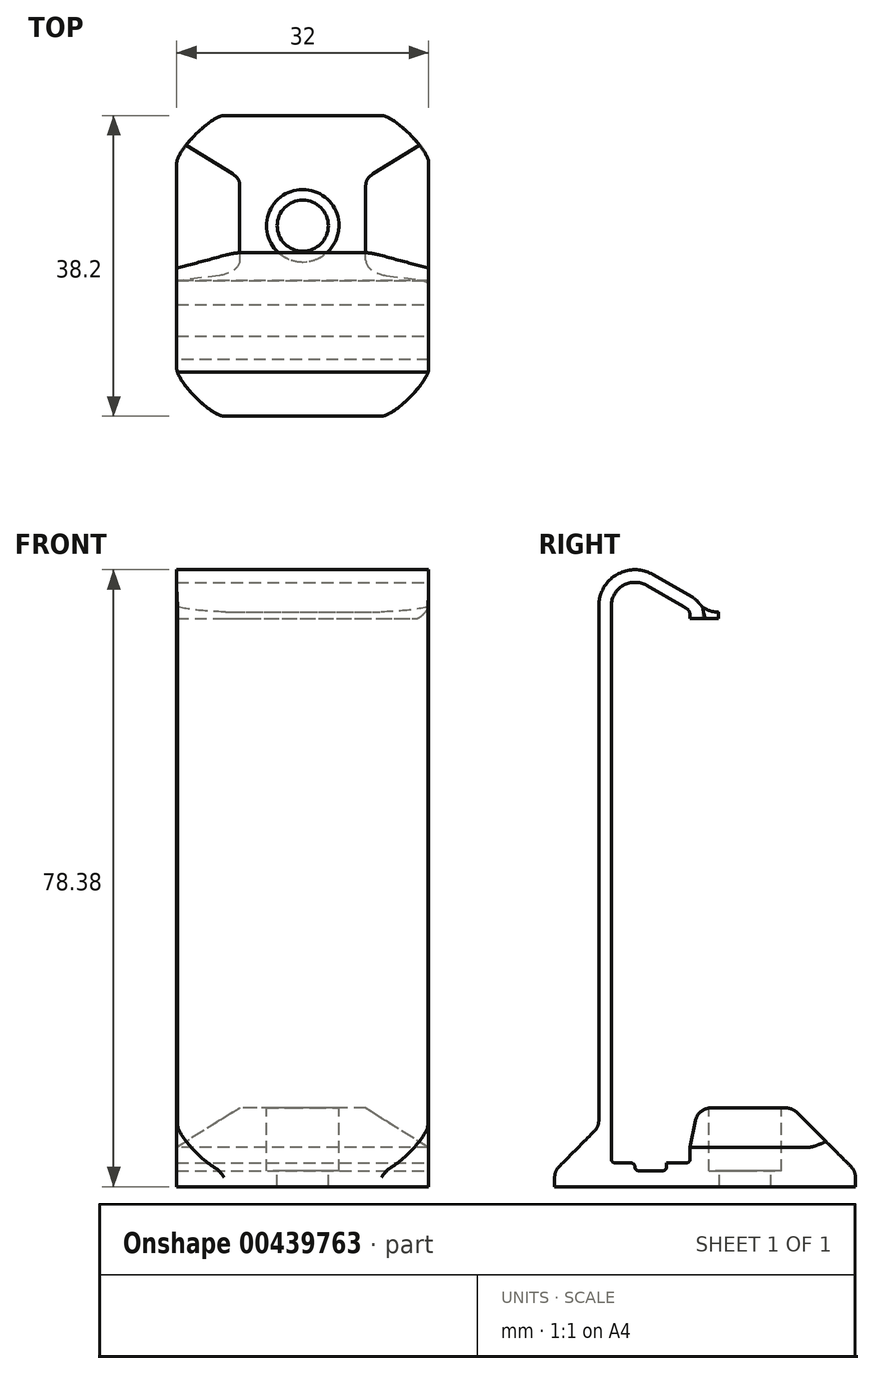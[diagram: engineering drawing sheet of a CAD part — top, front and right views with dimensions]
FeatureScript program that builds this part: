
annotation { "Feature Type Name" : "Feature", "Feature Type Description" : "" }
export const myFeature = defineFeature(function(context is Context, id is Id, definition is map)
    precondition{}
    {
        {
            var Q0;
            Q0=qCreatedBy(makeId("Right.planeOp"),FACE);
            var sketch = newSketch(context, id + "F0", { "sketchPlane" : qUnion([Q0])});
            skLineSegment(sketch, "E0.bottom", {"start": v(-5, 0) * mm, "end": v(5, 0) * mm});
            skLineSegment(sketch, "E0.top", {"start": v(-5, 70.2) * mm, "end": v(5, 70.2) * mm});
            skLineSegment(sketch, "E0.left", {"start": v(-5, 0) * mm, "end": v(-5, 70.2) * mm});
            skLineSegment(sketch, "E0.right", {"start": v(5, 0) * mm, "end": v(5, 70.2) * mm});
            skSolve(sketch);
        }
        {
            var Q0;
            Q0=qCreatedBy(makeId("Right.planeOp"),FACE);
            var sketch = newSketch(context, id + "F1", { "sketchPlane" : qUnion([Q0])});
            skLineSegment(sketch, "E1", {"start": v(-5, 4.6) * mm, "end": v(-6.6, 4.6) * mm});
            skLineSegment(sketch, "E2", {"start": v(-6.6, 4.6) * mm, "end": v(-12.2, -1) * mm});
            skLineSegment(sketch, "E3", {"start": v(-12.2, -1) * mm, "end": v(-12.2, -3) * mm});
            skLineSegment(sketch, "E4", {"start": v(-12.2, -3) * mm, "end": v(26, -3) * mm});
            skLineSegment(sketch, "E5", {"start": v(26, -3) * mm, "end": v(26, -1) * mm});
            skLineSegment(sketch, "E6", {"start": v(26, -1) * mm, "end": v(18, 7) * mm});
            skLineSegment(sketch, "E7", {"start": v(18, 7) * mm, "end": v(5, 7) * mm});
            skLineSegment(sketch, "E8", {"start": v(5, 7) * mm, "end": v(5, 0) * mm});
            skLineSegment(sketch, "E9", {"start": v(5, 0) * mm, "end": v(-5, 0) * mm});
            skLineSegment(sketch, "E10", {"start": v(-5, 0) * mm, "end": v(-5, 4.6) * mm});
            skSolve(sketch);
        }
        {
            var Q0;
            Q0=qSketchRegion(id+"F1",true);
            extrude(context, id + "F2", {"entities" : qUnion([Q0]), "endBound" : BoundingType.SYMMETRIC, "depth" : 32 * mm});
        }
        {
            var Q0;
            Q0=makeQuery(id+"F2.opExtrude","CAP_FACE",FACE,{"disambiguationData":[OSD([sQuery(id+"F1.wireOp",EDGE,"E1"),sQuery(id+"F1.wireOp",EDGE,"E2"),sQuery(id+"F1.wireOp",EDGE,"E3"),sQuery(id+"F1.wireOp",EDGE,"E4"),sQuery(id+"F1.wireOp",EDGE,"E5"),sQuery(id+"F1.wireOp",EDGE,"E6"),sQuery(id+"F1.wireOp",EDGE,"E7"),sQuery(id+"F1.wireOp",EDGE,"E8"),sQuery(id+"F1.wireOp",EDGE,"E9"),sQuery(id+"F1.wireOp",EDGE,"E10")])],"isStart":false});
            var sketch = newSketch(context, id + "F3", { "sketchPlane" : qUnion([Q0])});
            skLineSegment(sketch, "E11", {"start": v(-6.6, 4.6) * mm, "end": v(-5, 4.6) * mm});
            skLineSegment(sketch, "E12", {"start": v(-5, 4.6) * mm, "end": v(-5, 70.78) * mm});
            skLineSegment(sketch, "E13", {"start": v(-0.5, 73.38) * mm, "end": v(4.5, 70.49) * mm});
            skLineSegment(sketch, "E14", {"start": v(5, 69.62) * mm, "end": v(5, 69.2) * mm});
            skLineSegment(sketch, "E15", {"start": v(5, 69.2) * mm, "end": v(6.6, 69.2) * mm});
            skLineSegment(sketch, "E16", {"start": v(6.6, 69.2) * mm, "end": v(6.6, 69.62) * mm});
            skLineSegment(sketch, "E17", {"start": v(5.3, 71.87) * mm, "end": v(0.3, 74.76) * mm});
            skLineSegment(sketch, "E18", {"start": v(-6.6, 70.78) * mm, "end": v(-6.6, 4.6) * mm});
            skArc(sketch, "E19", {"start": v(-0.5, 73.38) * mm, "mid": v(-3.5, 73.38) * mm, "end": v(-5, 70.78) * mm});
            skArc(sketch, "E20", {"start": v(0.3, 74.76) * mm, "mid": v(-4.3, 74.76) * mm, "end": v(-6.6, 70.78) * mm});
            skArc(sketch, "E21", {"start": v(6.6, 69.62) * mm, "mid": v(6.25, 70.92) * mm, "end": v(5.3, 71.87) * mm});
            skArc(sketch, "E22", {"start": v(5, 69.62) * mm, "mid": v(4.87, 70.12) * mm, "end": v(4.5, 70.49) * mm});
            skLineSegment(sketch, "E23", {"start": v(4.5, 70.49) * mm, "end": v(5, 70.2) * mm, "construction": true});
            skLineSegment(sketch, "E24", {"start": v(5, 70.2) * mm, "end": v(5, 69.62) * mm, "construction": true});
            skLineSegment(sketch, "E25", {"start": v(5, 70.2) * mm, "end": v(-5, 70.78) * mm, "construction": true});
            skSolve(sketch);
        }
        {
            var Q0;
            Q0=qSketchRegion(id+"F3",true);
            var Q1;
            Q1=makeQuery(id+"F2.opExtrude","CAP_FACE",FACE,{"disambiguationData":[OSD([sQuery(id+"F1.wireOp",EDGE,"E1"),sQuery(id+"F1.wireOp",EDGE,"E2"),sQuery(id+"F1.wireOp",EDGE,"E3"),sQuery(id+"F1.wireOp",EDGE,"E4"),sQuery(id+"F1.wireOp",EDGE,"E5"),sQuery(id+"F1.wireOp",EDGE,"E6"),sQuery(id+"F1.wireOp",EDGE,"E7"),sQuery(id+"F1.wireOp",EDGE,"E8"),sQuery(id+"F1.wireOp",EDGE,"E9"),sQuery(id+"F1.wireOp",EDGE,"E10")])],"isStart":true});
            extrude(context, id + "F4", {"entities" : qUnion([Q0]), "operationType" : NewBodyOperationType.ADD, "endBound" : BoundingType.UP_TO_SURFACE, "oppositeDirection" : true, "endBoundEntityFace" : qUnion([Q1]), "depth" : 25 * mm});
        }
        {
            var Q0;
            Q0=makeQuery(id+"F4.boolean.opBoolean","MERGE",FACE,{"derivedFrom":[makeQuery(id+"F2.opExtrude","CAP_FACE",FACE,{"disambiguationData":[OSD([sQuery(id+"F1.wireOp",EDGE,"E1"),sQuery(id+"F1.wireOp",EDGE,"E2"),sQuery(id+"F1.wireOp",EDGE,"E3"),sQuery(id+"F1.wireOp",EDGE,"E4"),sQuery(id+"F1.wireOp",EDGE,"E5"),sQuery(id+"F1.wireOp",EDGE,"E6"),sQuery(id+"F1.wireOp",EDGE,"E7"),sQuery(id+"F1.wireOp",EDGE,"E8"),sQuery(id+"F1.wireOp",EDGE,"E9"),sQuery(id+"F1.wireOp",EDGE,"E10")])],"isStart":false}),makeQuery(id+"F4.opExtrude","CAP_FACE",FACE,{"disambiguationData":[OSD([sQuery(id+"F3.wireOp",EDGE,"E11"),sQuery(id+"F3.wireOp",EDGE,"E12"),sQuery(id+"F3.wireOp",EDGE,"E13"),sQuery(id+"F3.wireOp",EDGE,"E14"),sQuery(id+"F3.wireOp",EDGE,"E15"),sQuery(id+"F3.wireOp",EDGE,"E16"),sQuery(id+"F3.wireOp",EDGE,"E17"),sQuery(id+"F3.wireOp",EDGE,"E18"),sQuery(id+"F3.wireOp",EDGE,"E19"),sQuery(id+"F3.wireOp",EDGE,"E20"),sQuery(id+"F3.wireOp",EDGE,"E21"),sQuery(id+"F3.wireOp",EDGE,"E22")])],"isStart":true})]});
            var sketch = newSketch(context, id + "F5", { "sketchPlane" : qUnion([Q0])});
            skLineSegment(sketch, "E26.bottom", {"start": v(-2, 0) * mm, "end": v(2, 0) * mm});
            skLineSegment(sketch, "E26.top", {"start": v(-2, -1) * mm, "end": v(2, -1) * mm});
            skLineSegment(sketch, "E26.left", {"start": v(-2, 0) * mm, "end": v(-2, -1) * mm});
            skLineSegment(sketch, "E26.right", {"start": v(2, 0) * mm, "end": v(2, -1) * mm});
            skLineSegment(sketch, "E27", {"start": v(-5, 0) * mm, "end": v(-2, 0) * mm});
            skLineSegment(sketch, "E28", {"start": v(2, 0) * mm, "end": v(5, 0) * mm});
            skSolve(sketch);
        }
        {
            var Q0;
            Q0=qSketchRegion(id+"F5",true);
            extrude(context, id + "F6", {"entities" : qUnion([Q0]), "operationType" : NewBodyOperationType.REMOVE, "endBound" : BoundingType.THROUGH_ALL, "oppositeDirection" : true, "depth" : 25 * mm});
        }
        {
            var Q0;
            Q0=makeQuery(id+"F2.opExtrude","SWEPT_EDGE",EDGE,{"disambiguationData":[OSD([sQuery(id+"F1.wireOp",EDGE,"E7"),sQuery(id+"F1.wireOp",EDGE,"E8")])]});
            chamfer(context, id + "F7", {"entities" : qUnion([Q0]), "chamferType" : ChamferType.TWO_OFFSETS, "width1" : 5 * mm, "oppositeDirection" : false, "width2" : 1 * mm, "tangentPropagation" : true});
        }
        {
            var Q0;
            Q0=makeQuery(id+"F2.opExtrude","SWEPT_FACE",FACE,{"disambiguationData":[OSD([sQuery(id+"F1.wireOp",EDGE,"E7")])]});
            var sketch = newSketch(context, id + "F8", { "sketchPlane" : qUnion([Q0])});
            skCircle(sketch, "E29", {"center": v(0, 12) * mm, "radius": 4.6 * mm});
            skLineSegment(sketch, "E30", {"start": v(0, 7.4) * mm, "end": v(0, 6) * mm, "construction": true});
            skLineSegment(sketch, "E31", {"start": v(0, 16.6) * mm, "end": v(0, 18) * mm, "construction": true});
            skSolve(sketch);
        }
        {
            var Q0;
            Q0=qSketchRegion(id+"F8",true);
            extrude(context, id + "F9", {"entities" : qUnion([Q0]), "operationType" : NewBodyOperationType.REMOVE, "oppositeDirection" : true, "depth" : 8 * mm});
        }
        {
            var Q0;
            Q0=makeQuery(id+"F9.boolean.opBoolean","COPY",FACE,{"derivedFrom":makeQuery(id+"F9.opExtrude","CAP_FACE",FACE,{"disambiguationData":[OSD([sQuery(id+"F8.wireOp",EDGE,"E29")])],"isStart":false})});
            var sketch = newSketch(context, id + "F10", { "sketchPlane" : qUnion([Q0])});
            skCircle(sketch, "E32", {"center": v(0, 12) * mm, "radius": 3.25 * mm});
            skSolve(sketch);
        }
        {
            var Q0;
            Q0=qSketchRegion(id+"F10",true);
            extrude(context, id + "F11", {"entities" : qUnion([Q0]), "operationType" : NewBodyOperationType.REMOVE, "endBound" : BoundingType.UP_TO_NEXT, "oppositeDirection" : true, "depth" : 25 * mm});
        }
        {
            var Q0;
            Q0=makeQuery(id+"F2.opExtrude","SWEPT_EDGE",EDGE,{"disambiguationData":[OSD([sQuery(id+"F1.wireOp",EDGE,"E9"),sQuery(id+"F1.wireOp",EDGE,"E10")])]});
            var Q1;
            Q1=makeQuery(id+"F2.opExtrude","SWEPT_EDGE",EDGE,{"disambiguationData":[OSD([sQuery(id+"F1.wireOp",EDGE,"E8"),sQuery(id+"F1.wireOp",EDGE,"E9")])]});
            var Q2;
            Q2=makeQuery(id+"F2.opExtrude","SWEPT_EDGE",EDGE,{"disambiguationData":[OSD([sQuery(id+"F1.wireOp",EDGE,"E7"),sQuery(id+"F1.wireOp",EDGE,"E8")])]});
            var Q3;
            Q3=makeQuery(id+"F6.boolean.opBoolean","COPY",EDGE,{"derivedFrom":makeQuery(id+"F6.opExtrude","SWEPT_EDGE",EDGE,{"disambiguationData":[OSD([sQuery(id+"F5.wireOp",EDGE,"E26.top"),sQuery(id+"F5.wireOp",EDGE,"E26.right")])]})});
            var Q4;
            Q4=makeQuery(id+"F6.boolean.opBoolean","COPY",EDGE,{"derivedFrom":makeQuery(id+"F6.opExtrude","SWEPT_EDGE",EDGE,{"disambiguationData":[OSD([sQuery(id+"F5.wireOp",EDGE,"E26.top"),sQuery(id+"F5.wireOp",EDGE,"E26.left")])]})});
            var Q5;
            Q5=makeQuery(id+"F6.boolean.opBoolean","COPY",EDGE,{"derivedFrom":makeQuery(id+"F6.opExtrude","SWEPT_EDGE",EDGE,{"disambiguationData":[OSD([sQuery(id+"F5.wireOp",EDGE,"E26.bottom"),sQuery(id+"F5.wireOp",EDGE,"E26.right"),sQuery(id+"F5.wireOp",EDGE,"E28")])]})});
            var Q6;
            Q6=makeQuery(id+"F6.boolean.opBoolean","COPY",EDGE,{"derivedFrom":makeQuery(id+"F6.opExtrude","SWEPT_EDGE",EDGE,{"disambiguationData":[OSD([sQuery(id+"F5.wireOp",EDGE,"E26.bottom"),sQuery(id+"F5.wireOp",EDGE,"E26.left"),sQuery(id+"F5.wireOp",EDGE,"E27")])]})});
            fillet(context, id + "F12", {"entities" : qUnion([Q0, Q1, Q2, Q3, Q4, Q5, Q6]), "radius" : .5 * mm, "tangentPropagation" : true, "allowEdgeOverflow" : false});
        }
        {
            var Q0;
            Q0=makeQuery(id+"F2.opExtrude","SWEPT_EDGE",EDGE,{"disambiguationData":[OSD([sQuery(id+"F1.wireOp",EDGE,"E5"),sQuery(id+"F1.wireOp",EDGE,"E6")])]});
            var Q1;
            Q1=makeQuery(id+"F2.opExtrude","SWEPT_EDGE",EDGE,{"disambiguationData":[OSD([sQuery(id+"F1.wireOp",EDGE,"E6"),sQuery(id+"F1.wireOp",EDGE,"E7")])]});
            var Q2;
            {var subQ0=sQuery(id+"F1.wireOp",EDGE,"E2");Q2=makeQuery(id+"F4.boolean.opBoolean","MERGE",EDGE,{"derivedFrom":[makeQuery(id+"F2.opExtrude","SWEPT_EDGE",EDGE,{"disambiguationData":[OSD([sQuery(id+"F1.wireOp",EDGE,"E1"),subQ0])]}),makeQuery(id+"F4.opExtrude","SWEPT_EDGE",EDGE,{"disambiguationData":[OSD([subQ0,sQuery(id+"F3.wireOp",EDGE,"E11"),sQuery(id+"F3.wireOp",EDGE,"E18")])]})]});}
            var Q3;
            Q3=makeQuery(id+"F2.opExtrude","SWEPT_EDGE",EDGE,{"disambiguationData":[OSD([sQuery(id+"F1.wireOp",EDGE,"E2"),sQuery(id+"F1.wireOp",EDGE,"E3")])]});
            var Q4;
            {var subQ0=sQuery(id+"F1.wireOp",EDGE,"E7");Q4=makeQuery(id+"F7.opChamfer","BLEND_EDGE",EDGE,{"blendedFrom":[makeQuery(id+"F2.opExtrude","SWEPT_EDGE",EDGE,{"disambiguationData":[OSD([subQ0,sQuery(id+"F1.wireOp",EDGE,"E8")])]}),makeQuery(id+"F2.opExtrude","SWEPT_FACE",FACE,{"disambiguationData":[OSD([subQ0])]})],"blendedInto":[makeQuery(id+"F2.opExtrude","SWEPT_FACE",FACE,{"disambiguationData":[OSD([subQ0])]})]});}
            fillet(context, id + "F13", {"entities" : qUnion([Q0, Q1, Q2, Q3, Q4]), "radius" : 2 * mm, "tangentPropagation" : true, "allowEdgeOverflow" : false});
        }
        {
            var Q0;
            Q0=makeQuery(id+"F2.opExtrude","CAP_EDGE",EDGE,{"disambiguationData":[OSD([sQuery(id+"F1.wireOp",EDGE,"E3")])],"isStart":false});
            var Q1;
            Q1=makeQuery(id+"F2.opExtrude","CAP_EDGE",EDGE,{"disambiguationData":[OSD([sQuery(id+"F1.wireOp",EDGE,"E5")])],"isStart":false});
            var Q2;
            Q2=makeQuery(id+"F2.opExtrude","CAP_EDGE",EDGE,{"disambiguationData":[OSD([sQuery(id+"F1.wireOp",EDGE,"E5")])],"isStart":true});
            var Q3;
            Q3=makeQuery(id+"F2.opExtrude","CAP_EDGE",EDGE,{"disambiguationData":[OSD([sQuery(id+"F1.wireOp",EDGE,"E3")])],"isStart":true});
            fillet(context, id + "F14", {"entities" : qUnion([Q0, Q1, Q2, Q3]), "radius" : 6 * mm, "rho" : .2, "crossSection" : FilletCrossSection.CONIC, "allowEdgeOverflow" : false});
        }
        {
            var Q0;
            Q0=makeQuery(id+"F2.opExtrude","CAP_EDGE",EDGE,{"disambiguationData":[OSD([sQuery(id+"F1.wireOp",EDGE,"E7")])],"isStart":true});
            var Q1;
            Q1=makeQuery(id+"F2.opExtrude","CAP_EDGE",EDGE,{"disambiguationData":[OSD([sQuery(id+"F1.wireOp",EDGE,"E7")])],"isStart":false});
            chamfer(context, id + "F15", {"entities" : qUnion([Q0, Q1]), "chamferType" : ChamferType.TWO_OFFSETS, "width1" : 8 * mm, "oppositeDirection" : false, "width2" : 5 * mm});
        }
        {
            var Q0;
            Q0=makeQuery(id+"F4.opExtrude","SWEPT_FACE",FACE,{"disambiguationData":[OSD([sQuery(id+"F3.wireOp",EDGE,"E15")])]});
            var sketch = newSketch(context, id + "F16", { "sketchPlane" : qUnion([Q0])});
            skLineSegment(sketch, "E33", {"start": v(-16, -6.6) * mm, "end": v(-9.8, -8.26) * mm});
            skLineSegment(sketch, "E34", {"start": v(-7.22, -8.6) * mm, "end": v(7.22, -8.6) * mm});
            skLineSegment(sketch, "E35", {"start": v(9.8, -8.26) * mm, "end": v(16, -6.6) * mm});
            skPoint(sketch, "E36.visualSharp", {"position": v(8.54, -8.6) * mm});
            skArc(sketch, "E36.filletArc", {"start": v(7.22, -8.6) * mm, "mid": v(8.52, -8.51) * mm, "end": v(9.8, -8.26) * mm});
            skPoint(sketch, "E37.visualSharp", {"position": v(-8.54, -8.6) * mm});
            skArc(sketch, "E37.filletArc", {"start": v(-9.8, -8.26) * mm, "mid": v(-8.52, -8.51) * mm, "end": v(-7.22, -8.6) * mm});
            skLineSegment(sketch, "E38", {"start": v(16, -6.6) * mm, "end": v(16, -5) * mm});
            skLineSegment(sketch, "E39", {"start": v(16, -5) * mm, "end": v(-16, -5) * mm});
            skLineSegment(sketch, "E40", {"start": v(-16, -5) * mm, "end": v(-16, -6.6) * mm});
            skSolve(sketch);
        }
        {
            var Q0;
            Q0=qSketchRegion(id+"F16",true);
            extrude(context, id + "F17", {"entities" : qUnion([Q0]), "operationType" : NewBodyOperationType.ADD, "oppositeDirection" : true, "depth" : .8 * mm});
        }
        {
            var Q0;
            Q0=makeQuery(id+"F17.boolean.opBoolean","INTERSECT",EDGE,{"derivedFrom":[makeQuery(id+"F4.opExtrude","SWEPT_FACE",FACE,{"disambiguationData":[OSD([sQuery(id+"F3.wireOp",EDGE,"E21")])]}),makeQuery(id+"F17.opExtrude","CAP_FACE",FACE,{"disambiguationData":[OSD([sQuery(id+"F16.wireOp",EDGE,"E33"),sQuery(id+"F16.wireOp",EDGE,"E34"),sQuery(id+"F16.wireOp",EDGE,"E35"),sQuery(id+"F16.wireOp",EDGE,"E36.filletArc"),sQuery(id+"F16.wireOp",EDGE,"E37.filletArc"),sQuery(id+"F16.wireOp",EDGE,"E38"),sQuery(id+"F16.wireOp",EDGE,"E39"),sQuery(id+"F16.wireOp",EDGE,"E40")])],"isStart":false})]});
            fillet(context, id + "F18", {"entities" : qUnion([Q0]), "radius" : 3 * mm, "tangentPropagation" : true, "allowEdgeOverflow" : false});
        }
        {
            var Q0;
            Q0=makeQuery(id+"F4.opExtrude","CAP_EDGE",EDGE,{"disambiguationData":[OSD([sQuery(id+"F3.wireOp",EDGE,"E15")])],"isStart":true});
            var Q1;
            Q1=makeQuery(id+"F4.opExtrude","TWEAK_EDGE",EDGE,{"derivedFrom":[makeQuery(id+"F2.opExtrude","CAP_FACE",FACE,{"disambiguationData":[OSD([sQuery(id+"F1.wireOp",EDGE,"E1"),sQuery(id+"F1.wireOp",EDGE,"E2"),sQuery(id+"F1.wireOp",EDGE,"E3"),sQuery(id+"F1.wireOp",EDGE,"E4"),sQuery(id+"F1.wireOp",EDGE,"E5"),sQuery(id+"F1.wireOp",EDGE,"E6"),sQuery(id+"F1.wireOp",EDGE,"E7"),sQuery(id+"F1.wireOp",EDGE,"E8"),sQuery(id+"F1.wireOp",EDGE,"E9"),sQuery(id+"F1.wireOp",EDGE,"E10")])],"isStart":true}),makeQuery(id+"F3.imprint","IMPRINT",EDGE,{"derivedFrom":sQuery(id+"F3.wireOp",EDGE,"E15")})]});
            fillet(context, id + "F19", {"entities" : qUnion([Q0, Q1]), "radius" : 1.5 * mm, "tangentPropagation" : true, "rho" : .2, "crossSection" : FilletCrossSection.CONIC, "allowEdgeOverflow" : false});
        }
    });
